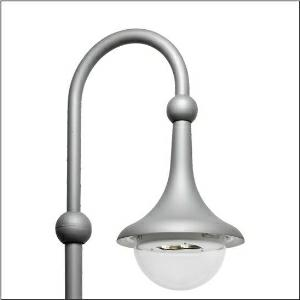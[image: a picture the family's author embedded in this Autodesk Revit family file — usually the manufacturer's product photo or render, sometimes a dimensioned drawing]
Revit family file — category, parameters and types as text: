
# Revit family: grosse_glocke_iq___st1_2a_5xa1565e1v108_00bb
name_source: partatom
category: Lighting Fixtures
units: mm (PartAtom-declared; Revit-internal decimal feet)

## family parameters
Cut with Voids When Loaded = No
Host = Face
Light Source = No
Part Type = Normal
Room Calculation Point = No
Round Connector Dimension = Use Diameter
Shared = No

## types (1)
- --- (1 x LED, 5180 lm, 34.3 W, 3000K)
    Apparent Load = 34 VA
    CIE Flux Codes = 28 66 95 100 100
    Color Rendering = 70
    Color Temperature = 3000K
    Default Elevation = 1800 mm
    Description = Large Bell iQ, mast luminaire, primary light control with 3 zone facetted reflector, of plastic, silver coated, primary optical cover: enclosure, of PMMA, transparent, light distribution: ST1.2a, light emission: direct distribution, primary light characteristic: asymmetric, installation type: suspended mounting, High Power LED, rated luminous flux: 5.180lm, luminous efficacy: 151lm/W, light colour: 730, colour temperature: 3000K, control gear: iQ-Street Remote, D4i with power reduction, control: optimised constant luminous flux control (CLO 2.0), Desk-Remote (wireless, voltage-free reading and setting of iQ features in the workshop via application-optimized NFC function/RFID function), Light-Fading, Smart-Wire, Night-Set, Lumen-Switch, Temp-Guard, Auto-Match, Street-Remote, pre-setting: logarithmic dimming characteristic, mains connection: 230..240V, AC, 50/60Hz, start of lifetime: 34W, end of service life: 38W, reduction: 16W, luminaire housing, bell-shaped, of glass-fibre reinforced polyester, coated, Siteco® metallic grey (DB 702S), please order curved mast extension separately, diameter: 530mm, height: 695mm, mounting height: 4..6m, Smart Interface above, protection rating (complete): IP54, insulation class (complete): insulation class II (safety insulation), certification: CE, ENEC, VDE, impact resistance: IK08, standard-compliant lighting for roads and squares, packaging unit: 1 piece

Light Distribution: ST1.2a
    Height = 695 mm
    Lamp = 1 x LED
    Lamp Light Flux = 5180 lm
    Lamp Power = 34.3 W
    Lamp count = 1
    Length = 530 mm
    Luminous efficacy = 151 lm/W
    Manufacturer = Siteco
    ModVariant = No
    Model = 5XA1565E1V108
    Number of Poles = 1
    OnlyDefault = Yes
    Power Factor = 1
    Product Name = Große Glocke iQ | ST1.2a
    Product group = mast luminaire | pylon annexe
    ProductGroupID = 6200
    Protection Class = Protection class II
    Protection Degree = IP 54
    RLX_Detail_Level = 1
    RLX_Emergency_Light_Flux = 0 lm
    RLX_Emergency_Type = 0
    RLX_Emergency_Type_DB = No
    RlxData = <blob elided: 71969 chars, md5=24c26bc6>
    Socket = socket
    Standby Power = 0 W
    System Light Flux = 5180 lm
    System Power = 34 W
    Type Comments = factory setting: luminous flux: 100 % | dim-lin: 254 | 640 mA
    Type Image = l_1347688.jpg
    URL = http://relux.com
    VarID = @adj_079867
    Voltage = 0 V
    Weight = 0.00 kg
    Width = 0 mm  [stored 0 ft]

note: [stored X ft] marks values corroborated as IEEE doubles in the binary element streams (Revit-internal decimal feet)

## geometry (parser evidence)
native form markers: Blend x4, Sweep x9
no freeform markers — native parametric forms only
